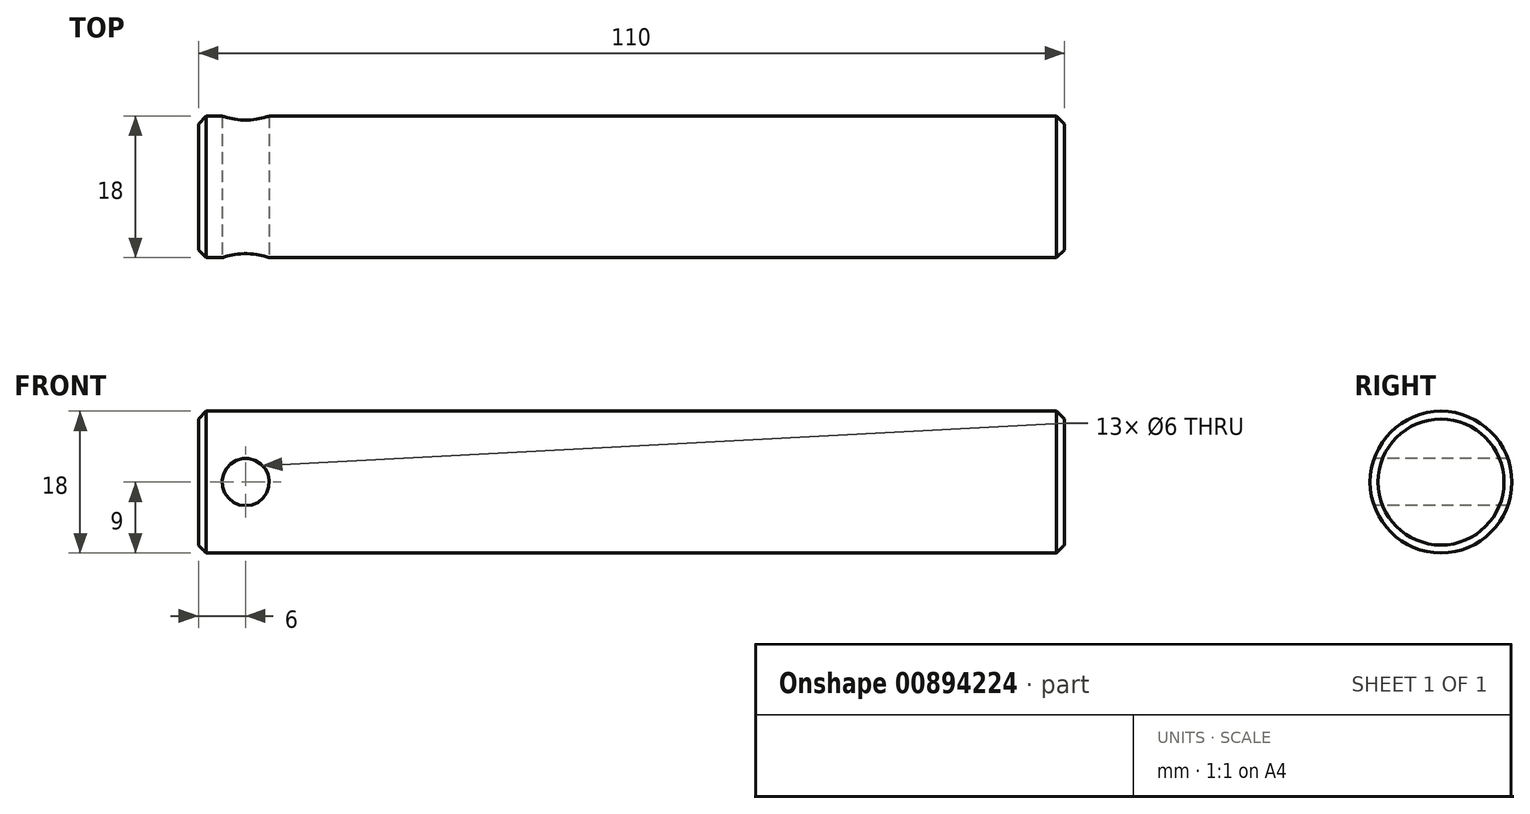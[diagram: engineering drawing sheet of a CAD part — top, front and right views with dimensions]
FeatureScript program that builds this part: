
annotation { "Feature Type Name" : "Feature", "Feature Type Description" : "" }
export const myFeature = defineFeature(function(context is Context, id is Id, definition is map)
    precondition{}
    {
        {
            var Q0;
            Q0=qCreatedBy(makeId("Right.planeOp"),FACE);
            var sketch = newSketch(context, id + "F0", { "sketchPlane" : qUnion([Q0])});
            skCircle(sketch, "E0", {"center": v(0, 0) * mm, "radius": 9 * mm});
            skSolve(sketch);
        }
        {
            var Q0;
            Q0=makeQuery(id+"F0.imprint","IMPRINT",FACE,{"disambiguationData":[TD([[makeQuery(id+"F0.imprint","IMPRINT",EDGE,{"derivedFrom":sQuery(id+"F0.wireOp",EDGE,"E0")}),1.0]])]});
            extrude(context, id + "F1", {"entities" : qUnion([Q0]), "depth" : 110 * mm, "offsetDistance" : 25 * mm});
        }
        {
            var Q0;
            Q0=makeQuery(id+"F1.opExtrude","CAP_EDGE",EDGE,{"disambiguationData":[OSD([sQuery(id+"F0.wireOp",EDGE,"E0")])],"isStart":false});
            var Q1;
            Q1=makeQuery(id+"F1.opExtrude","CAP_EDGE",EDGE,{"disambiguationData":[OSD([sQuery(id+"F0.wireOp",EDGE,"E0")])],"isStart":true});
            chamfer(context, id + "F2", {"entities" : qUnion([Q0, Q1]), "width" : 1 * mm, "tangentPropagation" : true});
        }
        {
            var Q0;
            Q0=qCreatedBy(makeId("Front.planeOp"),FACE);
            var sketch = newSketch(context, id + "F3", { "sketchPlane" : qUnion([Q0])});
            skCircle(sketch, "E1", {"center": v(6, 0) * mm, "radius": 3 * mm});
            skSolve(sketch);
        }
        {
            var Q0;
            Q0 = qSketchRegion(id + "F3", true);
            extrude(context, id + "F4", {"entities" : qUnion([Q0]), "operationType" : NewBodyOperationType.REMOVE, "oppositeDirection" : true, "depth" : 18 * mm, "offsetDistance" : 25 * mm, "symmetric" : true});
        }
    });
